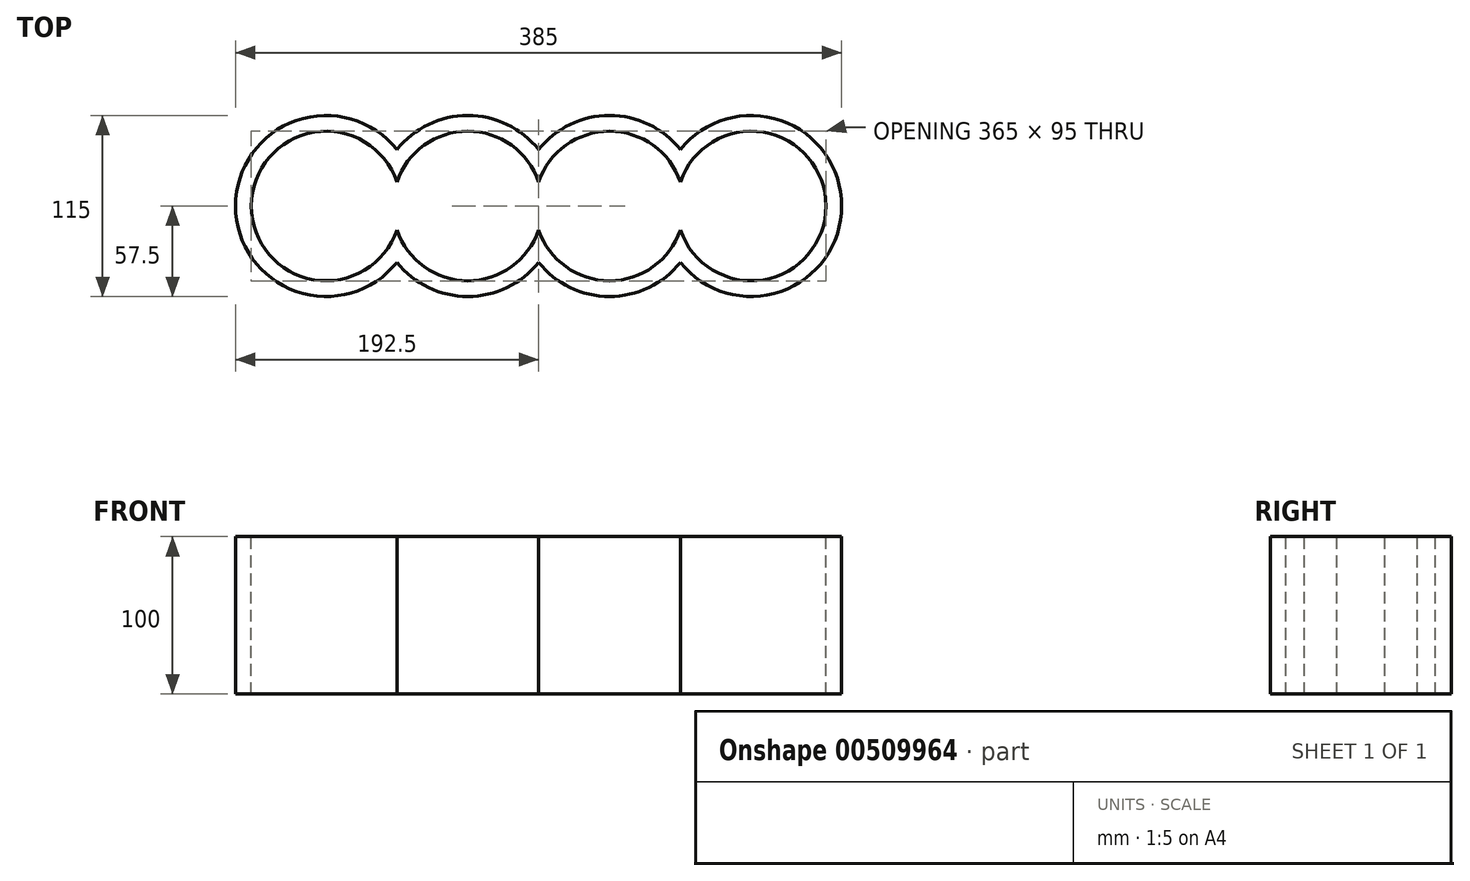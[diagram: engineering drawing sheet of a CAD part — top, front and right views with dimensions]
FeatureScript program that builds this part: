
annotation { "Feature Type Name" : "Feature", "Feature Type Description" : "" }
export const myFeature = defineFeature(function(context is Context, id is Id, definition is map)
    precondition{}
    {
        {
            var Q0;
            Q0=qCreatedBy(makeId("Top.planeOp"),FACE);
            var sketch = newSketch(context, id + "F0", { "sketchPlane" : qUnion([Q0])});
            skArc(sketch, "E0", {"start": v(-90, 15.2) * mm, "mid": v(-182.5, 0) * mm, "end": v(-90, -15.2) * mm});
            skArc(sketch, "E1", {"start": v(-90, -15.2) * mm, "mid": v(-45, -47.5) * mm, "end": v(0, -15.2) * mm});
            skArc(sketch, "E2", {"start": v(0, -15.2) * mm, "mid": v(45, -47.5) * mm, "end": v(90, -15.2) * mm});
            skArc(sketch, "E3", {"start": v(90, -15.2) * mm, "mid": v(182.5, 0) * mm, "end": v(90, 15.2) * mm});
            skArc(sketch, "E4.trimOffspring", {"start": v(0, 15.2) * mm, "mid": v(-45, 47.5) * mm, "end": v(-90, 15.2) * mm});
            skArc(sketch, "E5.trimOffspring", {"start": v(90, 15.2) * mm, "mid": v(45, 47.5) * mm, "end": v(0, 15.2) * mm});
            skArc(sketch, "E6", {"start": v(-90, 35.8) * mm, "mid": v(-192.5, 0) * mm, "end": v(-90, -35.8) * mm});
            skArc(sketch, "E7", {"start": v(-90, -35.8) * mm, "mid": v(-45, -57.5) * mm, "end": v(0, -35.8) * mm});
            skArc(sketch, "E8", {"start": v(0, -35.8) * mm, "mid": v(45, -57.5) * mm, "end": v(90, -35.8) * mm});
            skArc(sketch, "E9", {"start": v(90, -35.8) * mm, "mid": v(192.5, 0) * mm, "end": v(90, 35.8) * mm});
            skArc(sketch, "E10.trimOffspring", {"start": v(0, 35.8) * mm, "mid": v(-45, 57.5) * mm, "end": v(-90, 35.8) * mm});
            skArc(sketch, "E11.trimOffspring", {"start": v(90, 35.8) * mm, "mid": v(45, 57.5) * mm, "end": v(0, 35.8) * mm});
            skLineSegment(sketch, "E12.bottom", {"start": v(-241.26, 89.73) * mm, "end": v(220.55, 89.73) * mm});
            skLineSegment(sketch, "E12.top", {"start": v(-241.26, -99.29) * mm, "end": v(220.55, -99.29) * mm});
            skLineSegment(sketch, "E12.left", {"start": v(-241.26, 89.73) * mm, "end": v(-241.26, -99.29) * mm});
            skLineSegment(sketch, "E12.right", {"start": v(220.55, 89.73) * mm, "end": v(220.55, -99.29) * mm});
            skSolve(sketch);
        }
        {
            var Q0;
            Q0=makeQuery(id+"F0.imprint","IMPRINT",FACE,{"disambiguationData":[TD([[makeQuery(id+"F0.imprint","IMPRINT",EDGE,{"derivedFrom":sQuery(id+"F0.wireOp",EDGE,"E0")}),-1.0]])]});
            extrude(context, id + "F1", {"entities" : qUnion([Q0]), "oppositeDirection" : true, "depth" : 100 * mm});
        }
    });
